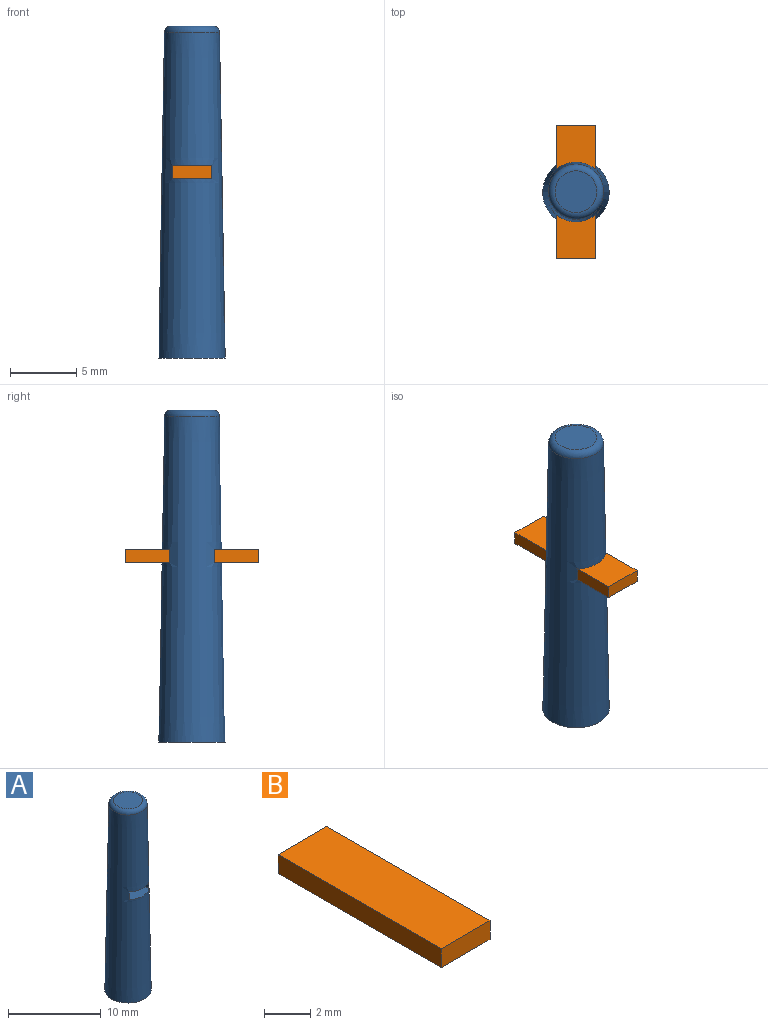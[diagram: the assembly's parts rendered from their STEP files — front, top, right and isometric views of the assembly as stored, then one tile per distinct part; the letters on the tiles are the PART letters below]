
ASSEMBLY  parts=2 mates=1
PART A: 8 faces, bbox 5x5x25 mm
  f0: cone r=2.5mm half-angle=1deg, axis (0,0,-1), area 345.5mm2, adj f2,f3,f4,f5,f6,f7
  f1: plane 3.14x3.14mm, normal (0,0,1), area 7.8mm2, adj f7
  f2: plane 5x5mm, normal (0,0,-1), area 19.6mm2, adj f0
  f3: plane 4.53x3mm, normal (0,0,1), area 12.5mm2, adj f0,f4,f6
  f4: plane 3.39x1mm, normal (-1,0,0), area 3.4mm2, adj f0,f3,f5
  f5: plane 4.49x3mm, normal (0,0,-1), area 12.4mm2, adj f0,f4,f6
  f6: plane 3.39x1mm, normal (1,0,0), area 3.4mm2, adj f0,f3,f5
  f7: torus R=1.57mm, axis (0,0,1), area 9.2mm2, adj f0,f1
PART B: 6 faces, bbox 3x10x1 mm
  f0: plane 10x1mm, normal (1,0,0), area 10mm2, adj f1,f3,f4,f5
  f1: plane 10x3mm, normal (0,0,1), area 30mm2, adj f0,f2,f4,f5
  f2: plane 10x1mm, normal (-1,0,0), area 10mm2, adj f1,f3,f4,f5
  f3: plane 10x3mm, normal (0,0,-1), area 30mm2, adj f0,f2,f4,f5
  f4: plane 3x1mm, normal (0,-1,0), area 3mm2, adj f0,f1,f2,f3
  f5: plane 3x1mm, normal (0,1,0), area 3mm2, adj f0,f1,f2,f3
PLACE A t=(-10.47,-6.63,-0.87)mm
PLACE B t=(-10.47,-1.63,13.11)mm
MATE planar B.f1 <-> A.f0  axis (0,0,1) through (-10.47,-6.63,13.61)mm
